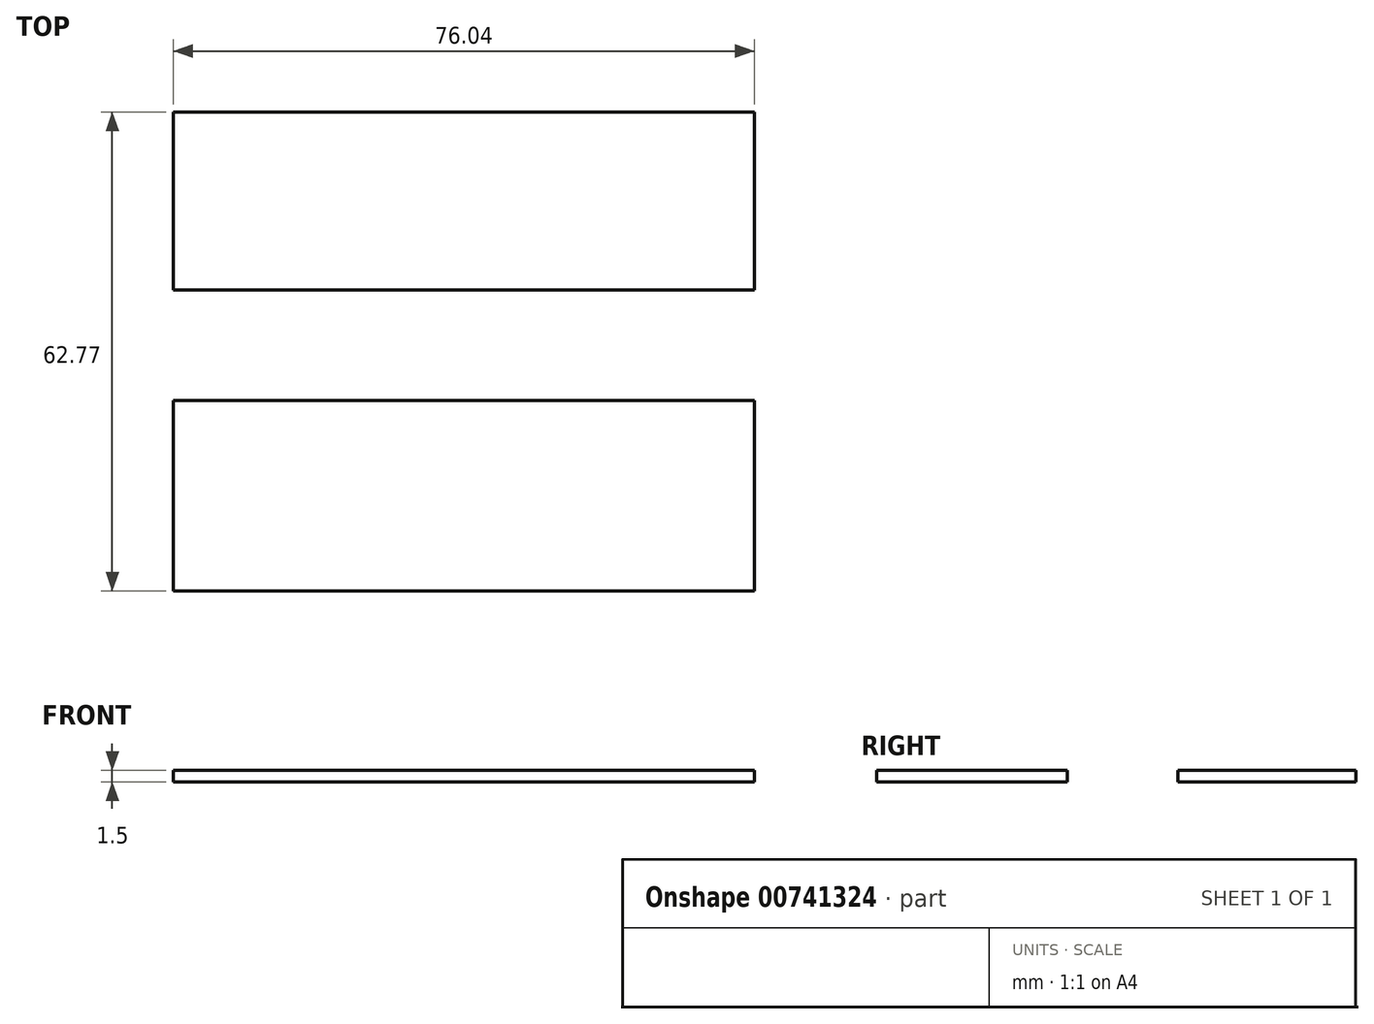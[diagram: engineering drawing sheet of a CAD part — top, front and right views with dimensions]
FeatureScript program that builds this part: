
annotation { "Feature Type Name" : "Feature", "Feature Type Description" : "" }
export const myFeature = defineFeature(function(context is Context, id is Id, definition is map)
    precondition{}
    {
        {
            var Q0;
            Q0=qCreatedBy(makeId("Top.planeOp"),FACE);
            var sketch = newSketch(context, id + "F0", { "sketchPlane" : qUnion([Q0])});
            skLineSegment(sketch, "E0.bottom", {"start": v(38.02, 12.47) * mm, "end": v(-38.02, 12.47) * mm});
            skLineSegment(sketch, "E0.top", {"start": v(38.02, -12.47) * mm, "end": v(-38.02, -12.47) * mm});
            skLineSegment(sketch, "E0.left", {"start": v(38.02, 12.47) * mm, "end": v(38.02, -12.47) * mm});
            skLineSegment(sketch, "E0.right", {"start": v(-38.02, 12.47) * mm, "end": v(-38.02, -12.47) * mm});
            skPoint(sketch, "E0.middle", {"position": v(0, 0) * mm});
            skLineSegment(sketch, "E1.bottom", {"start": v(38.02, 50.3) * mm, "end": v(-38.02, 50.3) * mm});
            skLineSegment(sketch, "E1.top", {"start": v(38.02, 27) * mm, "end": v(-38.02, 27) * mm});
            skLineSegment(sketch, "E1.left", {"start": v(38.02, 50.3) * mm, "end": v(38.02, 27) * mm});
            skLineSegment(sketch, "E1.right", {"start": v(-38.02, 50.3) * mm, "end": v(-38.02, 27) * mm});
            skPoint(sketch, "E1.middle", {"position": v(0, 38.65) * mm});
            skSolve(sketch);
        }
        {
            var Q0;
            Q0=makeQuery(id+"F0.imprint","IMPRINT",FACE,{"disambiguationData":[TD([[makeQuery(id+"F0.imprint","IMPRINT",EDGE,{"derivedFrom":sQuery(id+"F0.wireOp",EDGE,"E1.bottom")}),1.0]])]});
            var Q1;
            Q1=makeQuery(id+"F0.imprint","IMPRINT",FACE,{"disambiguationData":[TD([[makeQuery(id+"F0.imprint","IMPRINT",EDGE,{"derivedFrom":sQuery(id+"F0.wireOp",EDGE,"E0.bottom")}),1.0]])]});
            extrude(context, id + "F1", {"entities" : qUnion([Q0, Q1]), "depth" : 1.5 * mm, "offsetDistance" : 25.4 * mm});
        }
    });
